# Revit family: Haworth_PorcelainFlooringSystem
name_source: partatom
category: Generic Models
revit_build: Autodesk Revit Architecture 2014 (Build: 20130308_1515(x64)
units: mm (PartAtom-declared; Revit-internal decimal feet)

## types (2) — shared parameters
Chamfer Offset = 1/16"
Floor Thickness = 13/16"
Manufacturer = Haworth
Note = Verify Dimensions w/ Haworth
Panel Width Half = 11 99/128"
Revision Number = 1
Sustainability Info = http://www.haworth.com
Trim Finish = Haworth _ Polymer _ Fog
URL = http://www.haworth.com
URL - Product = http://www.haworth.com
Understructure Finish = Haworth _ Polymer _ Slate
Warranty = http://www.haworth.com

## per-type parameters (varying)
| type | Description | Model | Tile Only | Tile System |
| FBPV-PRS0-PA - Tile System | Haworth_PorcelainFlooringSystem - Tile System | FBPV-PRS0-PA | No | Yes |
| FBPV-PRS0-PG - Tile Only | Haworth_PorcelainFlooringSystem - Tile Only | FBPV-PRS0-PG | Yes | No |

## geometry (parser evidence)
native form markers: Sweep x3
no freeform markers — native parametric forms only
